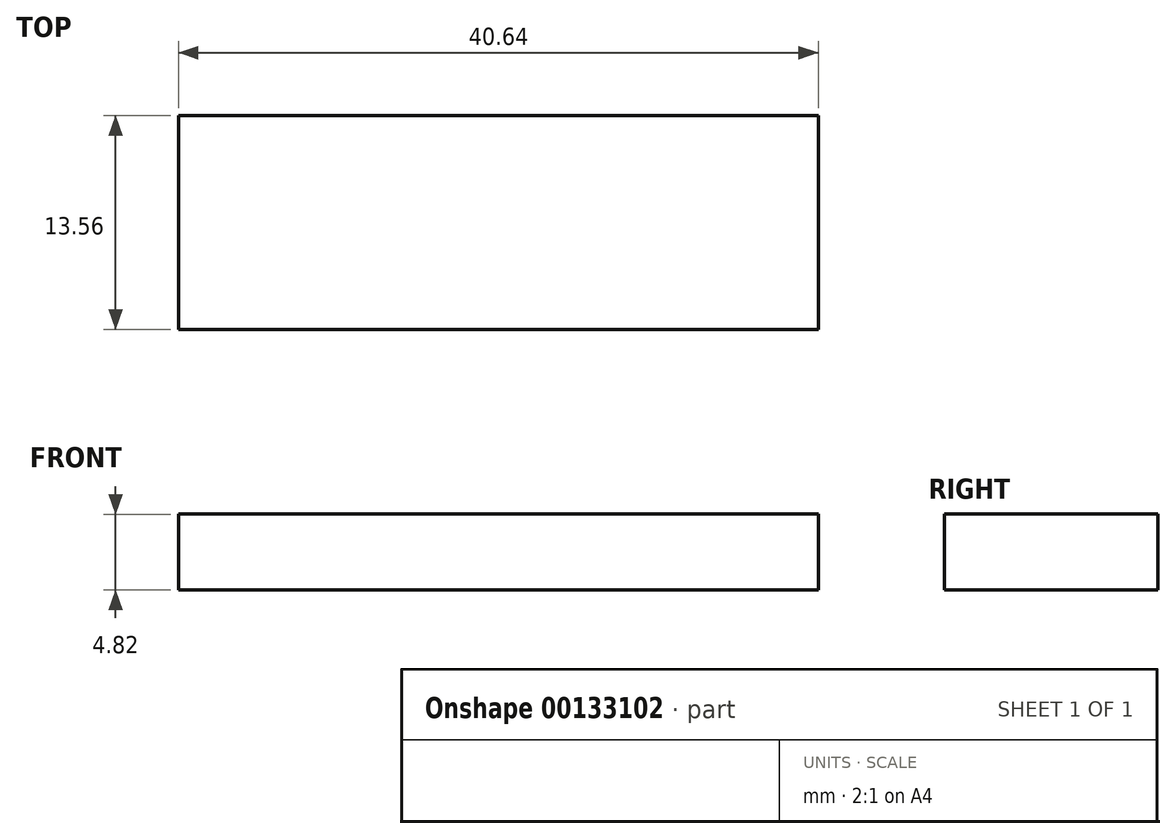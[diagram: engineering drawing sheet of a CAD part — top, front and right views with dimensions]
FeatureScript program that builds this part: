
annotation { "Feature Type Name" : "Feature", "Feature Type Description" : "" }
export const myFeature = defineFeature(function(context is Context, id is Id, definition is map)
    precondition{}
    {
        {
            var Q0;
            Q0=qCreatedBy(makeId("Top.planeOp"),FACE);
            var sketch = newSketch(context, id + "F0", { "sketchPlane" : qUnion([Q0])});
            skLineSegment(sketch, "E0.bottom", {"start": v(20.32, 6.78) * mm, "end": v(-20.32, 6.78) * mm});
            skLineSegment(sketch, "E0.top", {"start": v(20.32, -6.78) * mm, "end": v(-20.32, -6.78) * mm});
            skLineSegment(sketch, "E0.left", {"start": v(20.32, 6.78) * mm, "end": v(20.32, -6.78) * mm});
            skLineSegment(sketch, "E0.right", {"start": v(-20.32, 6.78) * mm, "end": v(-20.32, -6.78) * mm});
            skPoint(sketch, "E0.middle", {"position": v(0, 0) * mm});
            skSolve(sketch);
        }
        {
            var Q0;
            Q0 = qSketchRegion(id + "F0", true);
            extrude(context, id + "F1", {"entities" : qUnion([Q0]), "endBound" : BoundingType.SYMMETRIC, "depth" : 4.83 * mm});
        }
    });
